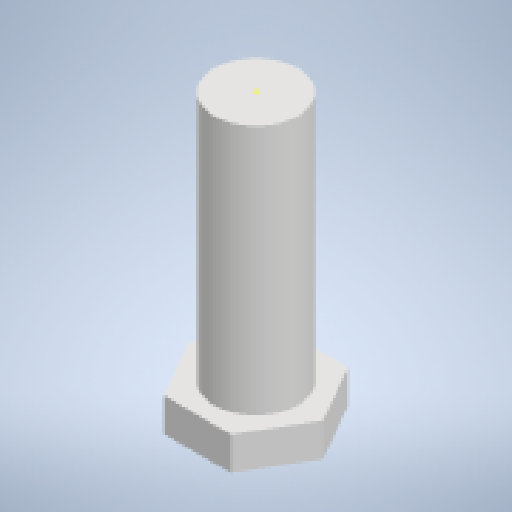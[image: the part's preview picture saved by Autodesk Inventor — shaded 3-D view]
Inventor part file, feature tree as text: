
AUTODESK INVENTOR PART (.ipt)
format: ipt  version: 2023 (Build 270158000, 158)  size: 139,776 bytes
history: native  units: in
note: dims shown in document units (in); Inventor stores cm internally (conversion verified against a paired STEP export)
features: sketch x3, extrude x2
ambient origin geometry x8: Origin, YZ Plane, XZ Plane, XY Plane, X Axis, Y Axis, Z Axis, Center Point
bodies: Solid1 (feature_tree)
feature tree (5):
  extrude  "Extrusion1"  Depth=0.0787in TaperAngle=0.0deg
  extrude  "Extrusion2"  Depth=0.5906in TaperAngle=0.0deg
  sketch  "Sketch3"
  sketch  "Sketch1"  dims[d0=0.2756in d1=0.0787in d2=0.0in]
  sketch  "Sketch2"  dims[d3=0.1969in d4=0.5906in d5=0.0in]
